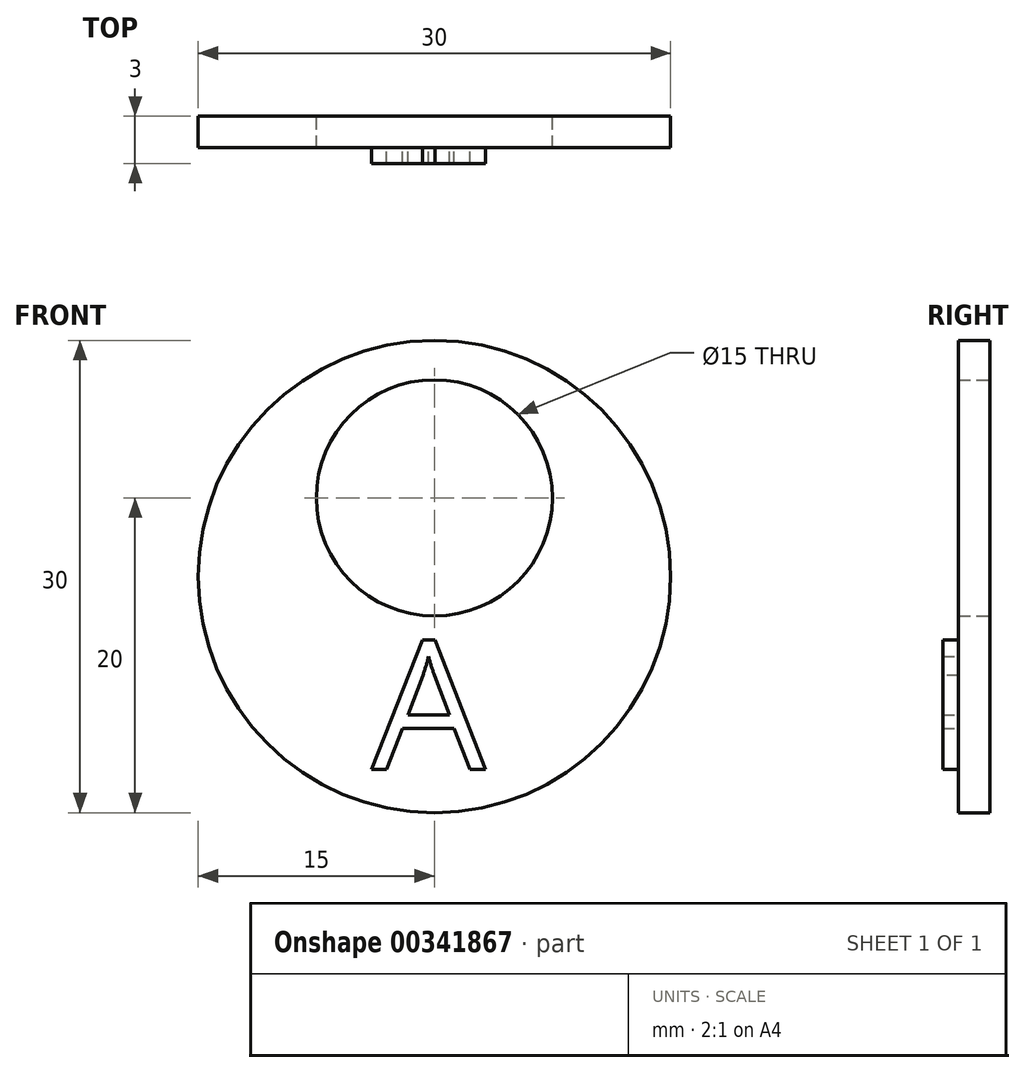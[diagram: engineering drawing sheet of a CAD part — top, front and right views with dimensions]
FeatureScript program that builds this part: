
annotation { "Feature Type Name" : "Feature", "Feature Type Description" : "" }
export const myFeature = defineFeature(function(context is Context, id is Id, definition is map)
    precondition{}
    {
        {
            var Q0;
            Q0=qCreatedBy(makeId("Front.planeOp"),FACE);
            var sketch = newSketch(context, id + "F0", { "sketchPlane" : qUnion([Q0])});
            skCircle(sketch, "E0", {"center": v(0, 0) * mm, "radius": 15 * mm});
            skPoint(sketch, "E1", {"position": v(0, 5) * mm});
            skCircle(sketch, "E2", {"center": v(0, 5) * mm, "radius": 7.5 * mm});
            skSolve(sketch);
        }
        {
            var Q0;
            Q0=makeQuery(id+"F0.imprint","IMPRINT",FACE,{"disambiguationData":[TD([[makeQuery(id+"F0.imprint","IMPRINT",EDGE,{"derivedFrom":sQuery(id+"F0.wireOp",EDGE,"E0")}),1.0]])]});
            extrude(context, id + "F1", {"entities" : qUnion([Q0]), "depth" : 2 * mm});
        }
        {
            var Q0;
            Q0=makeQuery(id+"F1.opExtrude","CAP_FACE",FACE,{"disambiguationData":[OSD([sQuery(id+"F0.wireOp",EDGE,"E0"),sQuery(id+"F0.wireOp",EDGE,"E2")])],"isStart":false});
            var sketch = newSketch(context, id + "F2", { "sketchPlane" : qUnion([Q0])});
            skText(sketch, "E3", { "text": "A", "fontName": "OpenSans-Regular.ttf"});
            const initialGuessF2  = {"E3": [-0.004, -0.01226, 1, 0, 0.00826]};
            skSetInitialGuess(sketch, initialGuessF2);
            skSolve(sketch);
        }
        {
            var Q0;
            Q0 = qSketchRegion(id + "F2", true);
            extrude(context, id + "F3", {"entities" : qUnion([Q0]), "operationType" : NewBodyOperationType.ADD, "depth" : 1 * mm});
        }
    });
